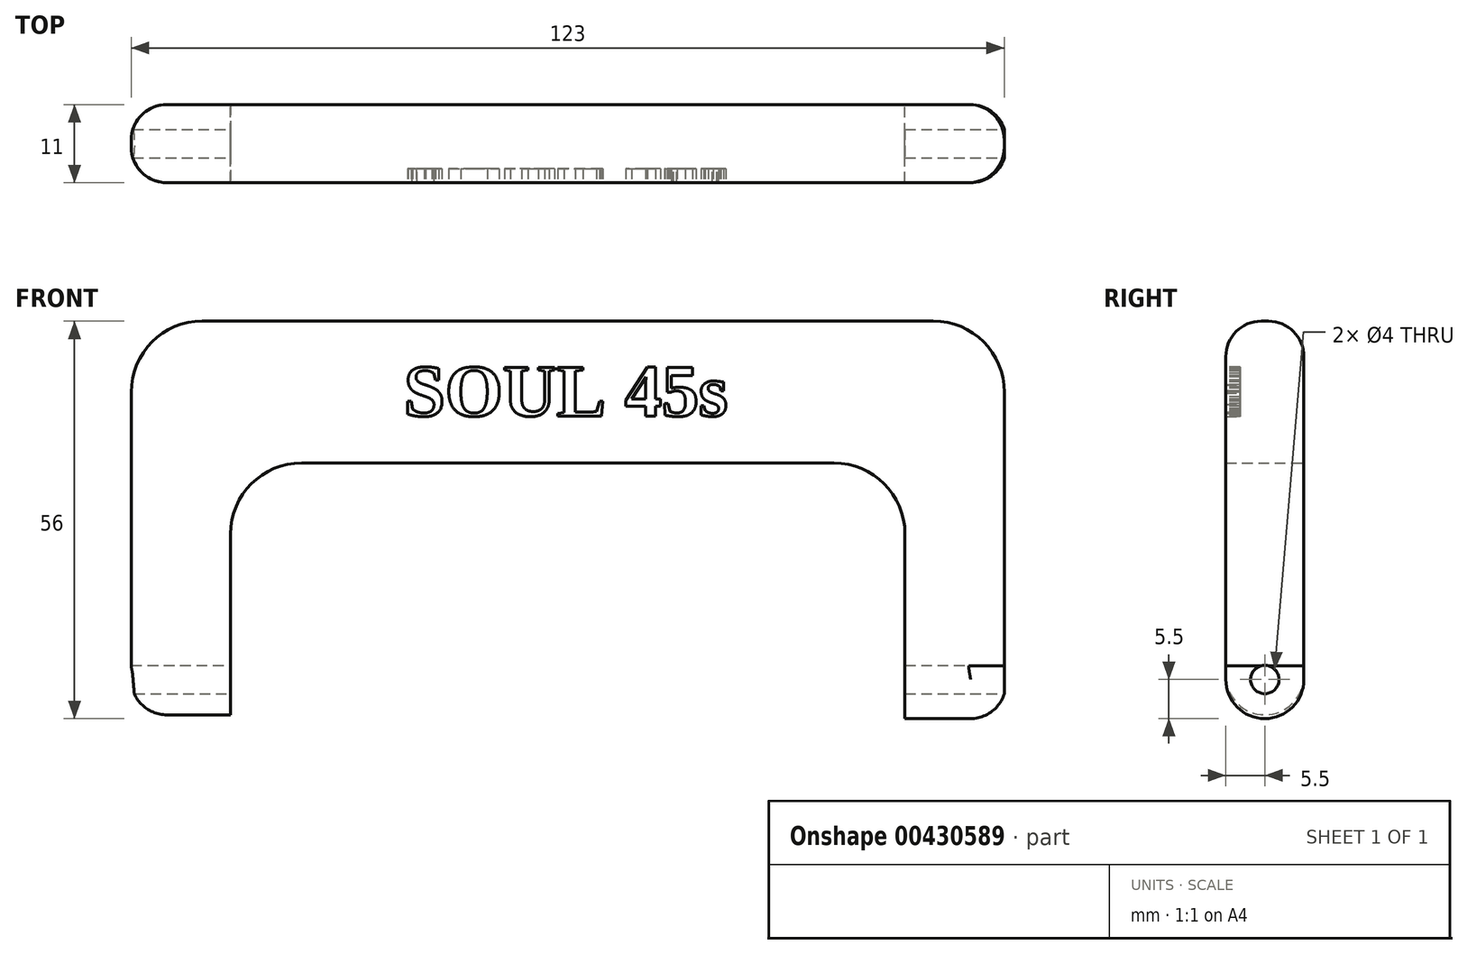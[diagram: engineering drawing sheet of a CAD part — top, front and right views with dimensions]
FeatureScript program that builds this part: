
annotation { "Feature Type Name" : "Feature", "Feature Type Description" : "" }
export const myFeature = defineFeature(function(context is Context, id is Id, definition is map)
    precondition{}
    {
        {
            var Q0;
            Q0=qCreatedBy(makeId("Front.planeOp"),FACE);
            var sketch = newSketch(context, id + "F0", { "sketchPlane" : qUnion([Q0])});
            skLineSegment(sketch, "E0", {"start": v(-59.28, -6.03) * mm, "end": v(-45.28, -6.03) * mm});
            skLineSegment(sketch, "E1", {"start": v(-45.28, -6.03) * mm, "end": v(-45.28, 4.97) * mm});
            skLineSegment(sketch, "E2", {"start": v(-45.28, 4.97) * mm, "end": v(-45.28, 16.12) * mm});
            skLineSegment(sketch, "E3", {"start": v(-35.28, 29.97) * mm, "end": v(-32.78, 29.97) * mm});
            skLineSegment(sketch, "E4", {"start": v(-32.78, 29.97) * mm, "end": v(14.32, 29.97) * mm});
            skLineSegment(sketch, "E5", {"start": v(14.32, 29.97) * mm, "end": v(39.72, 29.97) * mm});
            skLineSegment(sketch, "E6", {"start": v(49.72, 19.97) * mm, "end": v(49.72, 16.12) * mm});
            skLineSegment(sketch, "E7", {"start": v(49.72, 16.12) * mm, "end": v(49.72, 4.97) * mm});
            skLineSegment(sketch, "E8", {"start": v(49.72, 4.97) * mm, "end": v(49.72, -6.03) * mm});
            skLineSegment(sketch, "E9", {"start": v(49.72, -6.03) * mm, "end": v(63.72, -6.03) * mm});
            skLineSegment(sketch, "E10", {"start": v(63.72, -6.03) * mm, "end": v(63.72, 0) * mm});
            skLineSegment(sketch, "E11", {"start": v(63.72, 0) * mm, "end": v(63.72, 39.97) * mm});
            skLineSegment(sketch, "E12", {"start": v(53.72, 49.97) * mm, "end": v(-49.28, 49.97) * mm});
            skLineSegment(sketch, "E13", {"start": v(-59.28, 39.97) * mm, "end": v(-59.28, -6.03) * mm});
            skLineSegment(sketch, "E14", {"start": v(-45.28, 29.97) * mm, "end": v(49.72, 29.97) * mm});
            skLineSegment(sketch, "E15", {"start": v(-45.28, -6.03) * mm, "end": v(-45.28, 19.97) * mm});
            skPoint(sketch, "E16.visualSharp", {"position": v(-59.28, 49.97) * mm});
            skArc(sketch, "E16.filletArc", {"start": v(-49.28, 49.97) * mm, "mid": v(-56.35, 47.04) * mm, "end": v(-59.28, 39.97) * mm});
            skPoint(sketch, "E17.visualSharp", {"position": v(63.72, 49.97) * mm});
            skArc(sketch, "E17.filletArc", {"start": v(63.72, 39.97) * mm, "mid": v(60.8, 47.04) * mm, "end": v(53.72, 49.97) * mm});
            skPoint(sketch, "E18.visualSharp", {"position": v(49.72, 29.97) * mm});
            skArc(sketch, "E18.filletArc", {"start": v(49.72, 19.97) * mm, "mid": v(46.8, 27.04) * mm, "end": v(39.72, 29.97) * mm});
            skPoint(sketch, "E19.visualSharp", {"position": v(-45.28, 29.97) * mm});
            skArc(sketch, "E19.filletArc", {"start": v(-35.28, 29.97) * mm, "mid": v(-42.35, 27.04) * mm, "end": v(-45.28, 19.97) * mm});
            skSolve(sketch);
        }
        {
            var Q0;
            Q0=qCreatedBy(makeId("Right.planeOp"),FACE);
            var sketch = newSketch(context, id + "F1", { "sketchPlane" : qUnion([Q0])});
            skCircle(sketch, "E20", {"center": v(0, 0) * mm, "radius": 5.5 * mm});
            skLineSegment(sketch, "E21", {"start": v(0, 5.5) * mm, "end": v(0, 50.54) * mm});
            skLineSegment(sketch, "E22", {"start": v(-0.87, 49) * mm, "end": v(-5.5, 40.8) * mm});
            skLineSegment(sketch, "E23", {"start": v(-5.5, 40.8) * mm, "end": v(5.5, 40.8) * mm});
            skLineSegment(sketch, "E24", {"start": v(5.5, 40.8) * mm, "end": v(0.87, 49) * mm});
            skPoint(sketch, "E25.endSnap0", {"position": v(2.75, 45.67) * mm});
            skLineSegment(sketch, "E26", {"start": v(0, 40.8) * mm, "end": v(5.5, 40.8) * mm});
            skLineSegment(sketch, "E27", {"start": v(0, 40.8) * mm, "end": v(-5.5, 40.8) * mm});
            skLineSegment(sketch, "E28", {"start": v(5.5, 40.8) * mm, "end": v(5.5, 0) * mm});
            skLineSegment(sketch, "E29", {"start": v(-5.5, 40.8) * mm, "end": v(-5.5, 0) * mm});
            skPoint(sketch, "E30.visualSharp", {"position": v(0, 50.54) * mm});
            skArc(sketch, "E30.filletArc", {"start": v(0.87, 49) * mm, "mid": v(0, 49.5) * mm, "end": v(-0.87, 49) * mm});
            skCircle(sketch, "E31", {"center": v(0, 0) * mm, "radius": 12.65 * mm});
            skSolve(sketch);
        }
        {
            var Q0;
            Q0=makeQuery(id+"F0.imprint","IMPRINT",FACE,{"disambiguationData":[TD([[makeQuery(id+"F0.imprint","IMPRINT",EDGE,{"derivedFrom":sQuery(id+"F0.wireOp",EDGE,"E0")}),1.0]])]});
            extrude(context, id + "F2", {"entities" : qUnion([Q0]), "depth" : 5.5 * mm});
        }
        {
            var Q0;
            Q0=makeQuery(id+"F2.opExtrude","CAP_FACE",FACE,{"disambiguationData":[OSD([sQuery(id+"F0.wireOp",EDGE,"E0"),sQuery(id+"F0.wireOp",EDGE,"mhuuMDJj-kI9k-s3QC-w9C7-ezxL3k0Pu00q"),sQuery(id+"F0.wireOp",EDGE,"E6"),sQuery(id+"F0.wireOp",EDGE,"E7"),sQuery(id+"F0.wireOp",EDGE,"E8"),sQuery(id+"F0.wireOp",EDGE,"E9"),sQuery(id+"F0.wireOp",EDGE,"E10"),sQuery(id+"F0.wireOp",EDGE,"E11"),sQuery(id+"F0.wireOp",EDGE,"E12"),sQuery(id+"F0.wireOp",EDGE,"E13"),sQuery(id+"F0.wireOp",EDGE,"E14"),sQuery(id+"F0.wireOp",EDGE,"E15"),sQuery(id+"F0.wireOp",EDGE,"E16.filletArc"),sQuery(id+"F0.wireOp",EDGE,"E17.filletArc"),sQuery(id+"F0.wireOp",EDGE,"E18.filletArc")])],"isStart":true});
            extrude(context, id + "F3", {"entities" : qUnion([Q0]), "operationType" : NewBodyOperationType.ADD, "depth" : 5.5 * mm});
        }
        {
            var Q0;
            {var subQ0=sQuery(id+"F1.wireOp",EDGE,"E28");var subQ1=sQuery(id+"F1.wireOp",EDGE,"E20");var subQ2=makeQuery(id+"F1.imprint","INTERSECT",VERTEX,{"derivedFrom":[subQ1,subQ0]});Q0=makeQuery(id+"F1.imprint","IMPRINT",FACE,{"disambiguationData":[TD([[makeQuery(id+"F1.imprint","IMPRINT",EDGE,{"disambiguationData":[TD([[subQ2,1.0]])],"derivedFrom":subQ1}),-1.0]])]});}
            extrude(context, id + "F4", {"entities" : qUnion([Q0]), "operationType" : NewBodyOperationType.REMOVE, "oppositeDirection" : true, "depth" : 70 * mm});
        }
        {
            var Q0;
            {var subQ0=sQuery(id+"F0.wireOp",EDGE,"E11");var subQ1=sQuery(id+"F0.wireOp",EDGE,"E10");Q0=makeQuery(id+"F3.boolean.opBoolean","MERGE",FACE,{"derivedFrom":[makeQuery(id+"F2.opExtrude","SWEPT_FACE",FACE,{"disambiguationData":[OSD([subQ1,subQ0])]}),makeQuery(id+"F3.opExtrude","SWEPT_FACE",FACE,{"disambiguationData":[OSD([subQ1,subQ0])]})]});}
            var sketch = newSketch(context, id + "F5", { "sketchPlane" : qUnion([Q0])});
            skLineSegment(sketch, "E32", {"start": v(0, -6.03) * mm, "end": v(0, -0.53) * mm});
            skCircle(sketch, "E33", {"center": v(0, -0.53) * mm, "radius": 5.5 * mm});
            skCircle(sketch, "E34", {"center": v(0, -0.53) * mm, "radius": 10.2 * mm});
            skLineSegment(sketch, "E35", {"start": v(-5.5, -0.53) * mm, "end": v(-5.5, 8.05) * mm});
            skLineSegment(sketch, "E36", {"start": v(5.5, 0) * mm, "end": v(5.5, 8.05) * mm});
            skCircle(sketch, "E37", {"center": v(0, -0.53) * mm, "radius": 2 * mm});
            skSolve(sketch);
        }
        {
            var Q0;
            {var subQ0=sQuery(id+"F5.wireOp",EDGE,"E33");var subQ1=sQuery(id+"F0.wireOp",EDGE,"E10");var subQ5=makeQuery(id+"F2.opExtrude","CAP_EDGE",EDGE,{"disambiguationData":[OSD([subQ1,sQuery(id+"F0.wireOp",EDGE,"E11")])],"isStart":false});var subQ6=makeQuery(id+"F5.imprint","INTERSECT",VERTEX,{"derivedFrom":[subQ5,subQ0,sQuery(id+"F5.wireOp",EDGE,"E35")]});Q0=makeQuery(id+"F5.imprint","IMPRINT",FACE,{"disambiguationData":[TD([[makeQuery(id+"F5.imprint","IMPRINT",EDGE,{"disambiguationData":[TD([[subQ6,-1.0]])],"derivedFrom":subQ0}),-1.0]])]});}
            var Q1;
            {var subQ0=sQuery(id+"F5.wireOp",EDGE,"E33");var subQ1=sQuery(id+"F0.wireOp",EDGE,"E10");var subQ5=makeQuery(id+"F3.opExtrude","CAP_EDGE",EDGE,{"disambiguationData":[OSD([subQ1,sQuery(id+"F0.wireOp",EDGE,"E11")])],"isStart":false});var subQ6=makeQuery(id+"F5.imprint","INTERSECT",VERTEX,{"derivedFrom":[subQ5,subQ0]});Q1=makeQuery(id+"F5.imprint","IMPRINT",FACE,{"disambiguationData":[TD([[makeQuery(id+"F5.imprint","IMPRINT",EDGE,{"disambiguationData":[TD([[subQ6,1.0]])],"derivedFrom":subQ0}),-1.0]])]});}
            extrude(context, id + "F6", {"entities" : qUnion([Q0, Q1]), "operationType" : NewBodyOperationType.REMOVE, "oppositeDirection" : true, "depth" : 80 * mm});
        }
        {
            var Q0;
            Q0=makeQuery(id+"F5.imprint","IMPRINT",FACE,{"disambiguationData":[TD([[makeQuery(id+"F5.imprint","IMPRINT",EDGE,{"derivedFrom":sQuery(id+"F5.wireOp",EDGE,"E37")}),1.0]])]});
            extrude(context, id + "F7", {"entities" : qUnion([Q0]), "operationType" : NewBodyOperationType.REMOVE, "endBound" : BoundingType.THROUGH_ALL, "oppositeDirection" : true, "depth" : 25 * mm});
        }
        {
            var Q0;
            Q0=makeQuery(id+"F2.opExtrude","CAP_EDGE",EDGE,{"disambiguationData":[OSD([sQuery(id+"F0.wireOp",EDGE,"E12")])],"isStart":false});
            var Q1;
            Q1=makeQuery(id+"F2.opExtrude","CAP_EDGE",EDGE,{"disambiguationData":[OSD([sQuery(id+"F0.wireOp",EDGE,"E14")])],"isStart":false});
            fillet(context, id + "F8", {"entities" : qUnion([Q0, Q1]), "radius" : 5 * mm, "tangentPropagation" : true, "allowEdgeOverflow" : false});
        }
        {
            var Q0;
            Q0=makeQuery(id+"F2.opExtrude","CAP_FACE",FACE,{"disambiguationData":[OSD([sQuery(id+"F0.wireOp",EDGE,"E0"),sQuery(id+"F0.wireOp",EDGE,"E6"),sQuery(id+"F0.wireOp",EDGE,"E7"),sQuery(id+"F0.wireOp",EDGE,"E8"),sQuery(id+"F0.wireOp",EDGE,"E9"),sQuery(id+"F0.wireOp",EDGE,"E10"),sQuery(id+"F0.wireOp",EDGE,"E11"),sQuery(id+"F0.wireOp",EDGE,"E12"),sQuery(id+"F0.wireOp",EDGE,"E13"),sQuery(id+"F0.wireOp",EDGE,"E14"),sQuery(id+"F0.wireOp",EDGE,"E15"),sQuery(id+"F0.wireOp",EDGE,"E16.filletArc"),sQuery(id+"F0.wireOp",EDGE,"E17.filletArc"),sQuery(id+"F0.wireOp",EDGE,"E18.filletArc"),sQuery(id+"F0.wireOp",EDGE,"E19.filletArc")])],"isStart":false});
            var sketch = newSketch(context, id + "F9", { "sketchPlane" : qUnion([Q0])});
            skText(sketch, "E38", { "text": "SOUL 45s", "fontName": "Tinos-Bold.ttf"});
            const initialGuessF9  = {"E38": [-0.02087, 0.0366, 1, 0, 0.00753]};
            skSetInitialGuess(sketch, initialGuessF9);
            skSolve(sketch);
        }
        {
            var Q0;
            Q0 = qSketchRegion(id + "F9", true);
            extrude(context, id + "F10", {"entities" : qUnion([Q0]), "operationType" : NewBodyOperationType.REMOVE, "oppositeDirection" : true, "depth" : 2 * mm});
        }
    });
